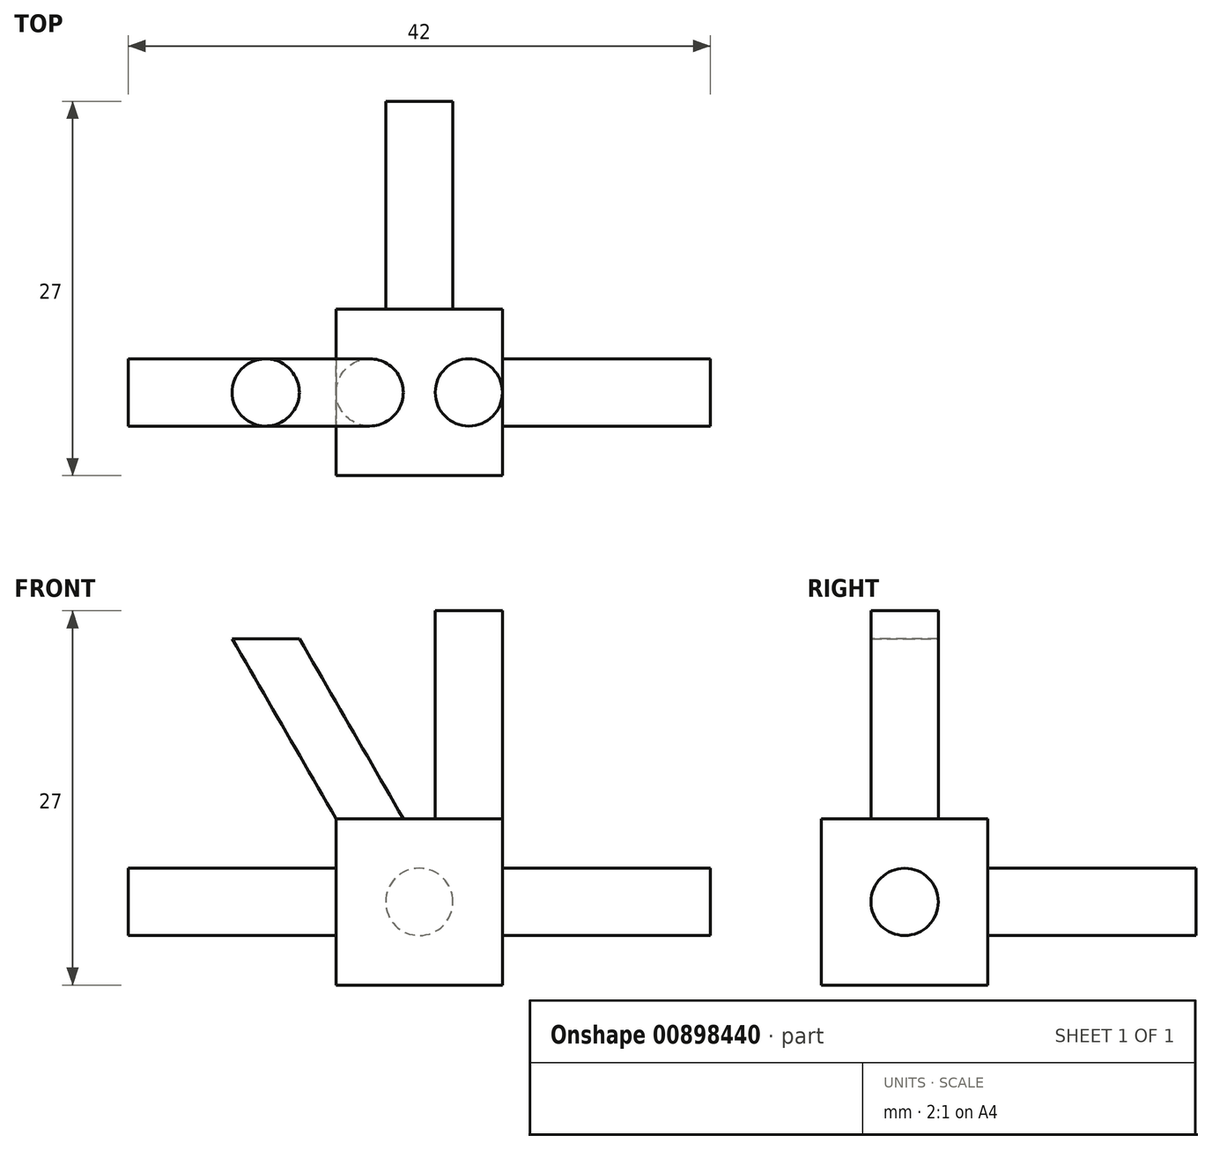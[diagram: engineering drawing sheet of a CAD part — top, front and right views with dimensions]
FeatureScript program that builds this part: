
annotation { "Feature Type Name" : "Feature", "Feature Type Description" : "" }
export const myFeature = defineFeature(function(context is Context, id is Id, definition is map)
    precondition{}
    {
        {
            var Q0;
            Q0=qCreatedBy(makeId("Top.planeOp"),FACE);
            var sketch = newSketch(context, id + "F0", { "sketchPlane" : qUnion([Q0])});
            skLineSegment(sketch, "E0", {"start": v(-22.31, 15.26) * mm, "end": v(-22.31, 3.26) * mm});
            skLineSegment(sketch, "E1", {"start": v(-22.31, 3.26) * mm, "end": v(-10.31, 3.26) * mm});
            skLineSegment(sketch, "E2", {"start": v(-10.31, 3.26) * mm, "end": v(-10.31, 15.26) * mm});
            skLineSegment(sketch, "E3", {"start": v(-10.31, 15.26) * mm, "end": v(-22.31, 15.26) * mm});
            skSolve(sketch);
        }
        {
            var Q0;
            Q0=qSketchRegion(id+"F0",true);
            extrude(context, id + "F1", {"entities" : qUnion([Q0]), "depth" : 12 * mm, "offsetDistance" : 25 * mm});
        }
        {
            var Q0;
            Q0=makeQuery(id+"F1.opExtrude","SWEPT_FACE",FACE,{"disambiguationData":[OSD([sQuery(id+"F0.wireOp",EDGE,"E2")])]});
            var sketch = newSketch(context, id + "F2", { "sketchPlane" : qUnion([Q0])});
            skCircle(sketch, "E4", {"center": v(9.26, 6) * mm, "radius": 2.43 * mm});
            skSolve(sketch);
        }
        {
            var Q0;
            Q0=makeQuery(id+"F2.imprint","IMPRINT",FACE,{"disambiguationData":[TD([[makeQuery(id+"F2.imprint","IMPRINT",EDGE,{"derivedFrom":sQuery(id+"F2.wireOp",EDGE,"E4")}),1.0]])]});
            extrude(context, id + "F3", {"entities" : qUnion([Q0]), "operationType" : NewBodyOperationType.ADD, "depth" : 15 * mm, "offsetDistance" : 25 * mm});
        }
        {
            var Q0;
            Q0=makeQuery(id+"F1.opExtrude","SWEPT_FACE",FACE,{"disambiguationData":[OSD([sQuery(id+"F0.wireOp",EDGE,"E0")])]});
            var sketch = newSketch(context, id + "F4", { "sketchPlane" : qUnion([Q0])});
            skCircle(sketch, "E5", {"center": v(-9.26, 6) * mm, "radius": 2.43 * mm});
            skSolve(sketch);
        }
        {
            var Q0;
            Q0=qSketchRegion(id+"F4",true);
            extrude(context, id + "F5", {"entities" : qUnion([Q0]), "operationType" : NewBodyOperationType.ADD, "depth" : 15 * mm, "offsetDistance" : 25 * mm});
        }
        {
            var Q0;
            Q0=makeQuery(id+"F1.opExtrude","CAP_FACE",FACE,{"disambiguationData":[OSD([sQuery(id+"F0.wireOp",EDGE,"E0"),sQuery(id+"F0.wireOp",EDGE,"E1"),sQuery(id+"F0.wireOp",EDGE,"E2"),sQuery(id+"F0.wireOp",EDGE,"E3")])],"isStart":false});
            var sketch = newSketch(context, id + "F6", { "sketchPlane" : qUnion([Q0])});
            skCircle(sketch, "E6", {"center": v(-19.89, 9.26) * mm, "radius": 2.43 * mm});
            skCircle(sketch, "E7", {"center": v(-12.74, 9.26) * mm, "radius": 2.43 * mm});
            skSolve(sketch);
        }
        {
            var Q0;
            Q0=makeQuery(id+"F1.opExtrude","SWEPT_FACE",FACE,{"disambiguationData":[OSD([sQuery(id+"F0.wireOp",EDGE,"E3")])]});
            var sketch = newSketch(context, id + "F7", { "sketchPlane" : qUnion([Q0])});
            skPoint(sketch, "E8.0", {"position": v(12.74, 12) * mm});
            skPoint(sketch, "E9.0", {"position": v(19.89, 12) * mm});
            skLineSegment(sketch, "E10", {"start": v(19.89, 12) * mm, "end": v(27.39, 25) * mm});
            skSolve(sketch);
        }
        {
            var Q0;
            Q0=makeQuery(id+"F6.imprint","IMPRINT",FACE,{"disambiguationData":[TD([[makeQuery(id+"F6.imprint","IMPRINT",EDGE,{"derivedFrom":sQuery(id+"F6.wireOp",EDGE,"E6")}),1.0]])]});
            var Q1;
            Q1=sQuery(id+"F7.wireOp",EDGE,"E10");
            sweep(context, id + "F8", {"operationType" : NewBodyOperationType.ADD, "profiles" : qUnion([Q0]), "path" : qUnion([Q1])});
        }
        {
            var Q0;
            Q0=qSketchRegion(id+"F7",true);
            var Q1;
            Q1=makeQuery(id+"F6.imprint","IMPRINT",FACE,{"disambiguationData":[TD([[makeQuery(id+"F6.imprint","IMPRINT",EDGE,{"derivedFrom":sQuery(id+"F6.wireOp",EDGE,"E7")}),1.0]])]});
            extrude(context, id + "F9", {"entities" : qUnion([Q0, Q1]), "operationType" : NewBodyOperationType.ADD, "depth" : 15 * mm, "offsetDistance" : 25 * mm});
        }
        {
            var Q0;
            {var subQ0=sQuery(id+"F0.wireOp",EDGE,"E3");Q0=makeQuery(id+"F7.imprint","IMPRINT",FACE,{"disambiguationData":[TD([[makeQuery(id+"F7.imprint","IMPRINT",EDGE,{"derivedFrom":makeQuery(id+"F1.opExtrude","CAP_EDGE",EDGE,{"disambiguationData":[OSD([subQ0])],"isStart":true})}),1.0]])]});}
            var sketch = newSketch(context, id + "F10", { "sketchPlane" : qUnion([Q0])});
            skCircle(sketch, "E11", {"center": v(16.31, 6) * mm, "radius": 2.43 * mm});
            skSolve(sketch);
        }
        {
            var Q0;
            Q0 = qSketchRegion(id + "F10", true);
            extrude(context, id + "F11", {"entities" : qUnion([Q0]), "operationType" : NewBodyOperationType.ADD, "depth" : 15 * mm, "offsetDistance" : 25 * mm});
        }
    });
